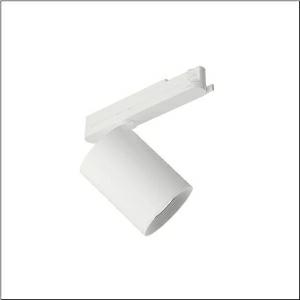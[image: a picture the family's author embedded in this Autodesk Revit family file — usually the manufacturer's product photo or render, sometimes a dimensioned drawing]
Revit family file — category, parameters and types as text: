
# Revit family: spot_21_51se14mbd5b
name_source: partatom
category: Lighting Fixtures
units: mm (PartAtom-declared; Revit-internal decimal feet)

## family parameters
Cut with Voids When Loaded = No
Host = Face
Light Source = No
Part Type = Normal
Room Calculation Point = No
Round Connector Dimension = Use Diameter
Shared = No

## types (1)
- --- (1 x LED, 5490 lm, 41.5 W, 4000K)
    Apparent Load = 42 VA
    CIE Flux Codes = 96 99 100 100 100
    Color Rendering = 90
    Color Temperature = 4000K
    Default Elevation = 1800 mm
    Description = Spot 21, directional spotlight, light control with lens, of PMMA, LED rated luminous flux: 5.270lm, light colour: 940, control gear: ECG Multilumen, with 3-phase adapter, mains connection: 220..240V, AC, 50/60Hz, of aluminium, traffic white (RAL 9016), length: 213mm, diameter: 105mm, protection rating (complete): IP20, insulation class (complete): insulation class I (protective earthing), certification: CE, impact resistance: IK02, permissible ambient temperature for indoor applications: -20..+40°C, packaging unit: 1 piece
    Height = 175 mm
    Lamp = 1 x LED
    Lamp Light Flux = 5490 lm
    Lamp Power = 41.5 W
    Lamp count = 1
    Length = 105 mm
    Luminous efficacy = 132 lm/W
    Manufacturer = Siteco
    ModVariant = No
    Model = 51SE14MBD5B
    Mounting Place = Ceiling
    Mounting Type = Pendant
    Number of Poles = 1
    OnlyDefault = Yes
    Power Factor = 1
    Product Name = Spot 21
    Product group = directional spotlight
    ProductGroupID = 905
    Protection Class = Protection class I
    Protection Degree = IP 20
    RLX_Detail_Level = 1
    RLX_Emergency_Light_Flux = 0 lm
    RLX_Emergency_Type = 0
    RLX_Emergency_Type_DB = No
    RlxData = <blob elided: 17621 chars, md5=f9f4328b>
    Socket = socket
    Standby Power = 0 W
    System Light Flux = 5490 lm
    System Power = 42 W
    Type Comments = factory setting: luminous flux: 100 % | (ON | ON | ON | ON) | 1050 mA
    Type Image = l_1003976.jpg
    URL = http://relux.com
    VarID = @adj_165089
    Voltage = 0 V
    Weight = 0.00 kg
    Width = 0 mm  [stored 0 ft]

note: [stored X ft] marks values corroborated as IEEE doubles in the binary element streams (Revit-internal decimal feet)

## geometry (parser evidence)
native form markers: Blend x4, Sweep x10
no freeform markers — native parametric forms only
